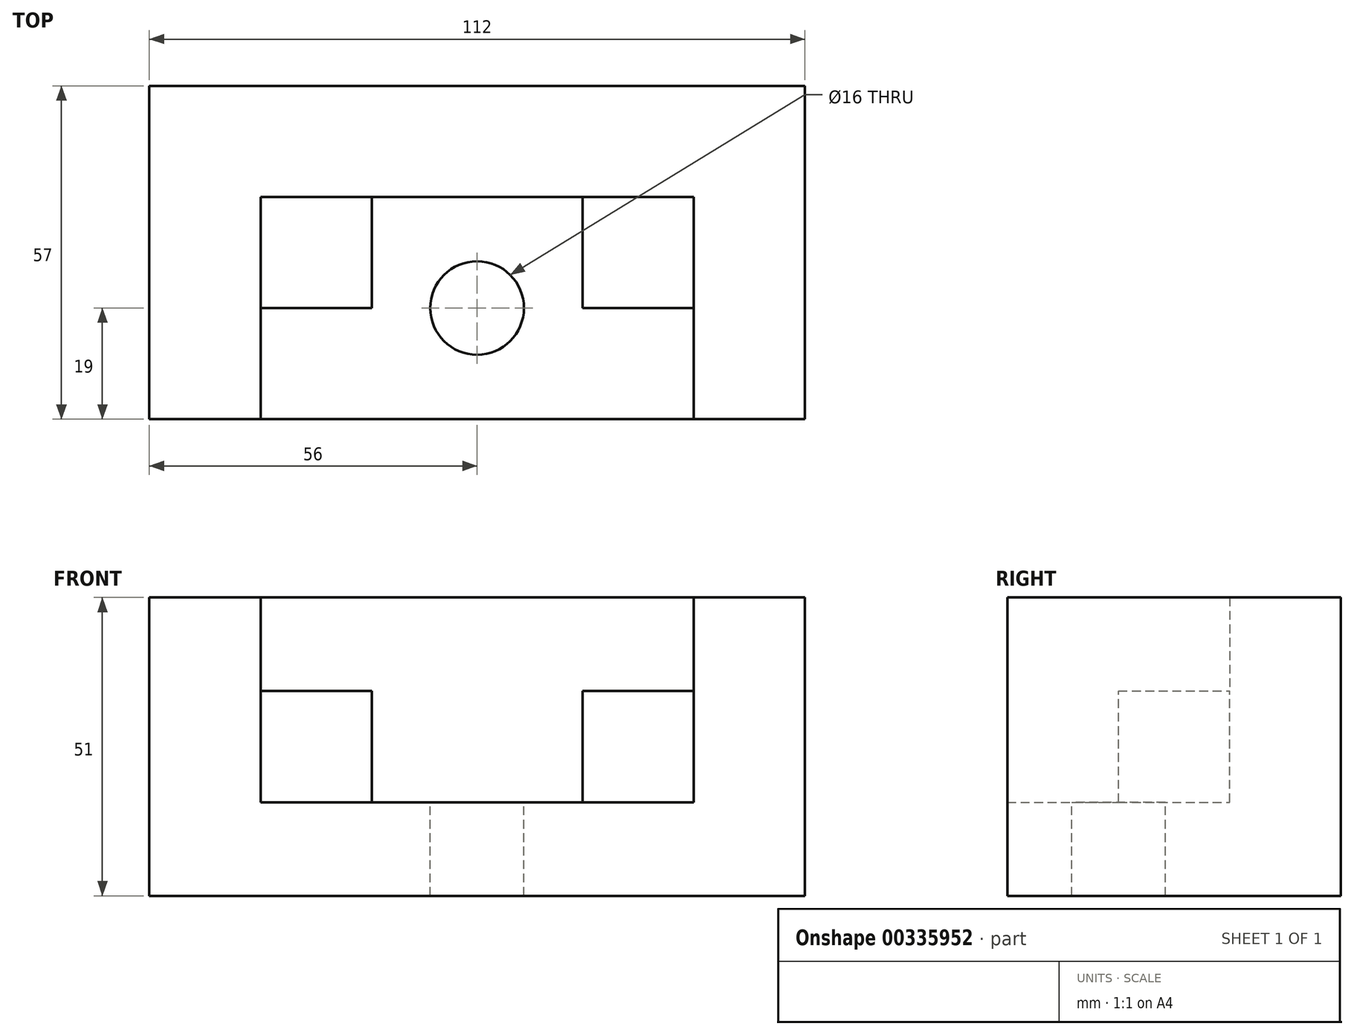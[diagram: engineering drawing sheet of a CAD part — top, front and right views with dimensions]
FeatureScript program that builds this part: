
annotation { "Feature Type Name" : "Feature", "Feature Type Description" : "" }
export const myFeature = defineFeature(function(context is Context, id is Id, definition is map)
    precondition{}
    {
        {
            var Q0;
            Q0=qCreatedBy(makeId("Right.planeOp"),FACE);
            var sketch = newSketch(context, id + "F0", { "sketchPlane" : qUnion([Q0])});
            skLineSegment(sketch, "E0", {"start": v(0, 0) * mm, "end": v(0, 16) * mm});
            skLineSegment(sketch, "E1", {"start": v(0, 0) * mm, "end": v(57, 0) * mm});
            skLineSegment(sketch, "E2", {"start": v(57, 0) * mm, "end": v(57, 51) * mm});
            skLineSegment(sketch, "E3", {"start": v(57, 51) * mm, "end": v(38, 51) * mm});
            skLineSegment(sketch, "E4", {"start": v(0, 16) * mm, "end": v(19, 16) * mm});
            skLineSegment(sketch, "E5", {"start": v(19, 16) * mm, "end": v(19, 35) * mm});
            skLineSegment(sketch, "E6", {"start": v(38, 51) * mm, "end": v(38, 35) * mm});
            skLineSegment(sketch, "E7", {"start": v(38, 35) * mm, "end": v(19, 35) * mm});
            skSolve(sketch);
        }
        {
            var Q0;
            Q0 = qSketchRegion(id + "F0", true);
            extrude(context, id + "F1", {"entities" : qUnion([Q0]), "endBound" : BoundingType.SYMMETRIC, "depth" : 74 * mm});
        }
        {
            var Q0;
            Q0=makeQuery(id+"F1.opExtrude","SWEPT_FACE",FACE,{"disambiguationData":[OSD([sQuery(id+"F0.wireOp",EDGE,"E7")])]});
            var sketch = newSketch(context, id + "F2", { "sketchPlane" : qUnion([Q0])});
            skLineSegment(sketch, "E8", {"start": v(-18, 19) * mm, "end": v(-18, 38) * mm});
            skLineSegment(sketch, "E9", {"start": v(18, 19) * mm, "end": v(18, 38) * mm});
            skLineSegment(sketch, "E10", {"start": v(-18, 38) * mm, "end": v(18, 38) * mm});
            skLineSegment(sketch, "E11", {"start": v(18, 19) * mm, "end": v(-18, 19) * mm});
            skLineSegment(sketch, "E12", {"start": v(-37, 38) * mm, "end": v(-18, 38) * mm, "construction": true});
            skLineSegment(sketch, "E13", {"start": v(-37, 19) * mm, "end": v(-37, 38) * mm, "construction": true});
            skLineSegment(sketch, "E14", {"start": v(-37, 19) * mm, "end": v(-18, 19) * mm, "construction": true});
            skLineSegment(sketch, "E15", {"start": v(-18, 38) * mm, "end": v(-18, 19) * mm, "construction": true});
            skSolve(sketch);
        }
        {
            var Q0;
            Q0 = qSketchRegion(id + "F2", true);
            extrude(context, id + "F3", {"entities" : qUnion([Q0]), "operationType" : NewBodyOperationType.REMOVE, "oppositeDirection" : true, "depth" : 19 * mm});
        }
        {
            var Q0;
            Q0=makeQuery(id+"F1.opExtrude","CAP_FACE",FACE,{"disambiguationData":[OSD([sQuery(id+"F0.wireOp",EDGE,"E0"),sQuery(id+"F0.wireOp",EDGE,"E1"),sQuery(id+"F0.wireOp",EDGE,"E2"),sQuery(id+"F0.wireOp",EDGE,"E3"),sQuery(id+"F0.wireOp",EDGE,"E4"),sQuery(id+"F0.wireOp",EDGE,"E5"),sQuery(id+"F0.wireOp",EDGE,"E6"),sQuery(id+"F0.wireOp",EDGE,"E7")])],"isStart":false});
            var sketch = newSketch(context, id + "F4", { "sketchPlane" : qUnion([Q0])});
            skLineSegment(sketch, "E16", {"start": v(57, 0) * mm, "end": v(57, 51) * mm});
            skLineSegment(sketch, "E17", {"start": v(57, 51) * mm, "end": v(0, 51) * mm});
            skLineSegment(sketch, "E18", {"start": v(0, 51) * mm, "end": v(0, 0) * mm});
            skLineSegment(sketch, "E19", {"start": v(0, 0) * mm, "end": v(57, 0) * mm});
            skSolve(sketch);
        }
        {
            var Q0;
            Q0 = qSketchRegion(id + "F4", true);
            extrude(context, id + "F5", {"entities" : qUnion([Q0]), "operationType" : NewBodyOperationType.ADD, "depth" : 19 * mm});
        }
        {
            var Q0;
            Q0=makeQuery(id+"F1.opExtrude","CAP_FACE",FACE,{"disambiguationData":[OSD([sQuery(id+"F0.wireOp",EDGE,"E0"),sQuery(id+"F0.wireOp",EDGE,"E1"),sQuery(id+"F0.wireOp",EDGE,"E2"),sQuery(id+"F0.wireOp",EDGE,"E3"),sQuery(id+"F0.wireOp",EDGE,"E4"),sQuery(id+"F0.wireOp",EDGE,"E5"),sQuery(id+"F0.wireOp",EDGE,"E6"),sQuery(id+"F0.wireOp",EDGE,"E7")])],"isStart":true});
            var sketch = newSketch(context, id + "F6", { "sketchPlane" : qUnion([Q0])});
            skLineSegment(sketch, "E20", {"start": v(-57, 0) * mm, "end": v(0, 0) * mm});
            skLineSegment(sketch, "E21", {"start": v(0, 0) * mm, "end": v(0, 51) * mm});
            skLineSegment(sketch, "E22", {"start": v(-57, 51) * mm, "end": v(0, 51) * mm});
            skLineSegment(sketch, "E23", {"start": v(-57, 51) * mm, "end": v(-57, 0) * mm});
            skSolve(sketch);
        }
        {
            var Q0;
            Q0 = qSketchRegion(id + "F6", true);
            extrude(context, id + "F7", {"entities" : qUnion([Q0]), "operationType" : NewBodyOperationType.ADD, "depth" : 19 * mm});
        }
        {
            var Q0;
            Q0=makeQuery(id+"F3.boolean.opBoolean","MERGE",FACE,{"derivedFrom":[makeQuery(id+"F1.opExtrude","SWEPT_FACE",FACE,{"disambiguationData":[OSD([sQuery(id+"F0.wireOp",EDGE,"E4")])]}),makeQuery(id+"F3.opExtrude","CAP_FACE",FACE,{"disambiguationData":[OSD([sQuery(id+"F2.wireOp",EDGE,"E8"),sQuery(id+"F2.wireOp",EDGE,"E9"),sQuery(id+"F2.wireOp",EDGE,"E10"),sQuery(id+"F2.wireOp",EDGE,"E11")])],"isStart":false})]});
            var sketch = newSketch(context, id + "F8", { "sketchPlane" : qUnion([Q0])});
            skCircle(sketch, "E24", {"center": v(0, 19) * mm, "radius": 8 * mm});
            skSolve(sketch);
        }
        {
            var Q0;
            Q0 = qSketchRegion(id + "F8", true);
            extrude(context, id + "F9", {"entities" : qUnion([Q0]), "operationType" : NewBodyOperationType.REMOVE, "oppositeDirection" : true, "depth" : 51 * mm});
        }
    });
